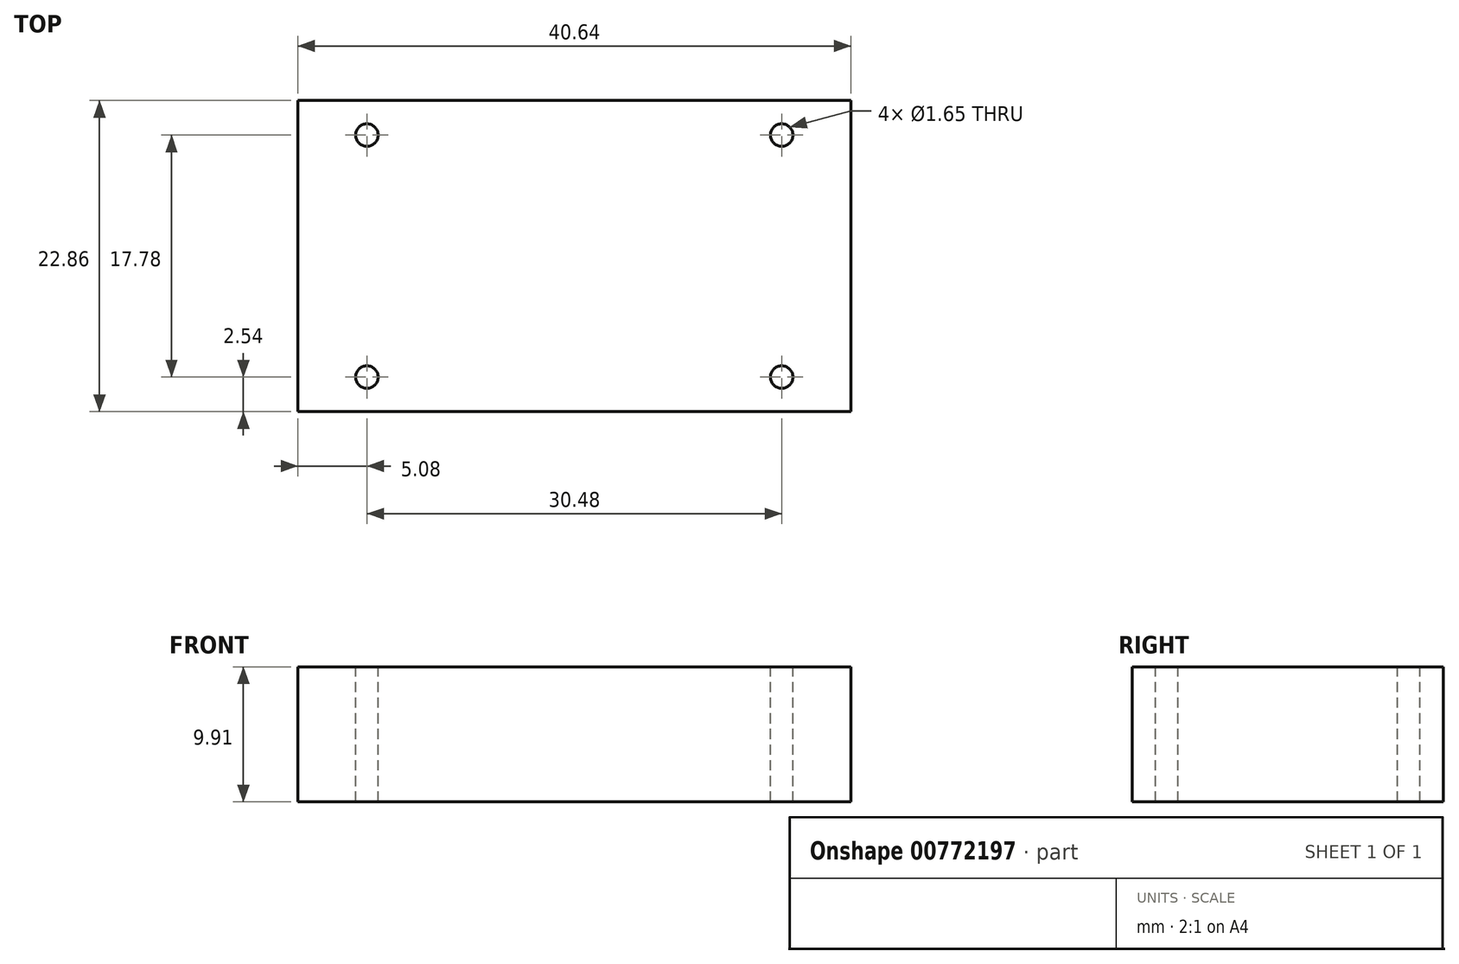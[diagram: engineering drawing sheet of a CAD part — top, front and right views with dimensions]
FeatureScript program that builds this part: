
annotation { "Feature Type Name" : "Feature", "Feature Type Description" : "" }
export const myFeature = defineFeature(function(context is Context, id is Id, definition is map)
    precondition{}
    {
        {
            var Q0;
            Q0=qCreatedBy(makeId("Top.planeOp"),FACE);
            var sketch = newSketch(context, id + "F0", { "sketchPlane" : qUnion([Q0])});
            skLineSegment(sketch, "E0.bottom", {"start": v(0, 0) * mm, "end": v(40.64, 0) * mm});
            skLineSegment(sketch, "E0.top", {"start": v(0, 22.86) * mm, "end": v(40.64, 22.86) * mm});
            skLineSegment(sketch, "E0.left", {"start": v(0, 0) * mm, "end": v(0, 22.86) * mm});
            skLineSegment(sketch, "E0.right", {"start": v(40.64, 0) * mm, "end": v(40.64, 22.86) * mm});
            skSolve(sketch);
        }
        {
            var Q0;
            Q0=makeQuery(id+"F0.imprint","IMPRINT",FACE,{"disambiguationData":[TD([[makeQuery(id+"F0.imprint","IMPRINT",EDGE,{"derivedFrom":sQuery(id+"F0.wireOp",EDGE,"E0.bottom")}),1.0]])]});
            extrude(context, id + "F1", {"entities" : qUnion([Q0]), "depth" : 9.9 * mm, "offsetDistance" : 25.4 * mm});
        }
        {
            var Q0;
            Q0=makeQuery(id+"F1.opExtrude","CAP_FACE",FACE,{"disambiguationData":[OSD([sQuery(id+"F0.wireOp",EDGE,"E0.bottom"),sQuery(id+"F0.wireOp",EDGE,"E0.top"),sQuery(id+"F0.wireOp",EDGE,"E0.left"),sQuery(id+"F0.wireOp",EDGE,"E0.right")])],"isStart":false});
            var sketch = newSketch(context, id + "F2", { "sketchPlane" : qUnion([Q0])});
            skCircle(sketch, "E1", {"center": v(5.08, 20.32) * mm, "radius": 0.83 * mm});
            skCircle(sketch, "E2", {"center": v(35.56, 20.32) * mm, "radius": 0.83 * mm});
            skCircle(sketch, "E3", {"center": v(35.56, 2.54) * mm, "radius": 0.83 * mm});
            skCircle(sketch, "E4", {"center": v(5.08, 2.54) * mm, "radius": 0.83 * mm});
            skSolve(sketch);
        }
        {
            var Q0;
            Q0=qSketchRegion(id+"F2",true);
            extrude(context, id + "F3", {"entities" : qUnion([Q0]), "operationType" : NewBodyOperationType.REMOVE, "endBound" : BoundingType.UP_TO_NEXT, "oppositeDirection" : true, "depth" : 25.4 * mm, "offsetDistance" : 25.4 * mm});
        }
    });
